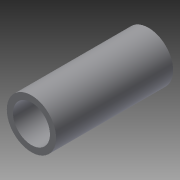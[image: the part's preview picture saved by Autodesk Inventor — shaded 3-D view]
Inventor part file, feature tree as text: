
AUTODESK INVENTOR PART (.ipt)
format: ipt  version: 2015 (Build 190159000, 159)  size: 78,848 bytes
history: native  units: mm
features: extrude x1, sketch x1
ambient origin geometry x8: Origin, YZ Plane, XZ Plane, XY Plane, X Axis, Y Axis, Z Axis, Center Point
bodies: Solid1 (feature_tree)
feature tree (2):
  extrude  "Extrusion1"  Depth=19.0mm
  sketch  "Sketch1"  dims[d0=8.0mm d1=6.0mm d2=19.0mm d3=0.0mm]
